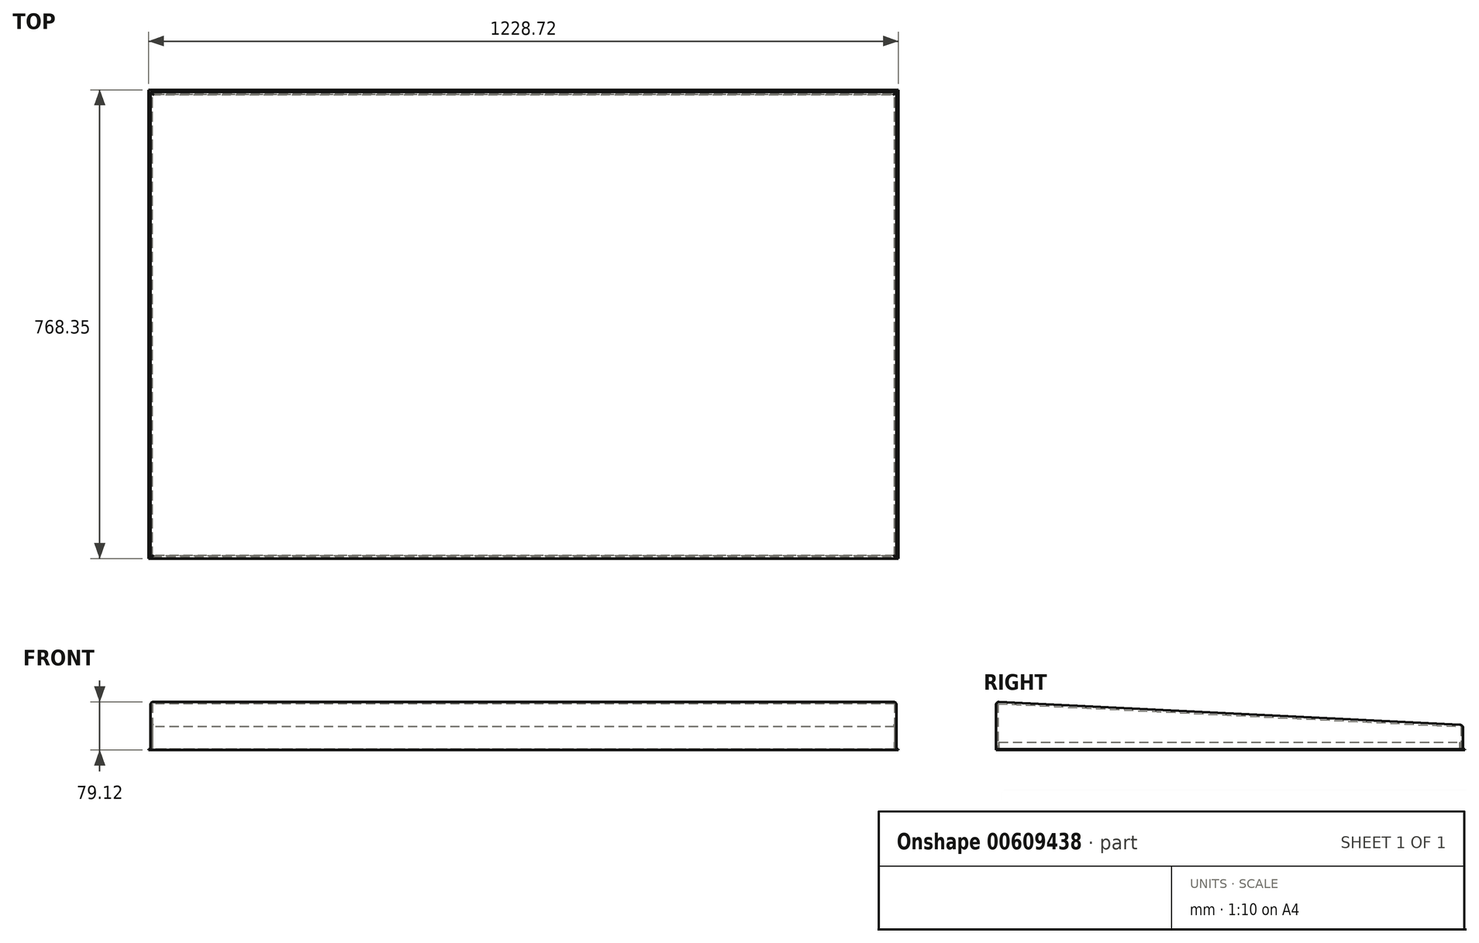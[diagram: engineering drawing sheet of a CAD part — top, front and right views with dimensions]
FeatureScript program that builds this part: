
annotation { "Feature Type Name" : "Feature", "Feature Type Description" : "" }
export const myFeature = defineFeature(function(context is Context, id is Id, definition is map)
    precondition{}
    {
        {
            var Q0;
            Q0=qCreatedBy(makeId("Top.planeOp"),FACE);
            var sketch = newSketch(context, id + "F0", { "sketchPlane" : qUnion([Q0])});
            skLineSegment(sketch, "E0.rect.bottom", {"start": v(611.19, 382.59) * mm, "end": v(-611.19, 382.59) * mm});
            skLineSegment(sketch, "E0.rect.top", {"start": v(611.19, -382.59) * mm, "end": v(-611.19, -382.59) * mm});
            skLineSegment(sketch, "E0.rect.left", {"start": v(611.19, 382.59) * mm, "end": v(611.19, -382.59) * mm});
            skLineSegment(sketch, "E0.rect.right", {"start": v(-611.19, 382.59) * mm, "end": v(-611.19, -382.59) * mm});
            skPoint(sketch, "E0.rect.middle", {"position": v(0, 0) * mm});
            skLineSegment(sketch, "E1.rect.bottom", {"start": v(-608.01, 379.41) * mm, "end": v(608.01, 379.41) * mm});
            skLineSegment(sketch, "E1.rect.top", {"start": v(-608.01, -379.41) * mm, "end": v(608.01, -379.41) * mm});
            skLineSegment(sketch, "E1.rect.left", {"start": v(-608.01, 379.41) * mm, "end": v(-608.01, -379.41) * mm});
            skLineSegment(sketch, "E1.rect.right", {"start": v(608.01, 379.41) * mm, "end": v(608.01, -379.41) * mm});
            skSolve(sketch);
        }
        {
            var Q0;
            Q0=makeQuery(id+"F0.imprint","IMPRINT",FACE,{"disambiguationData":[TD([[makeQuery(id+"F0.imprint","IMPRINT",EDGE,{"derivedFrom":sQuery(id+"F0.wireOp",EDGE,"E0.rect.bottom")}),1.0]])]});
            extrude(context, id + "F1", {"entities" : qUnion([Q0]), "depth" : 76.2 * mm});
        }
        {
            var Q0;
            Q0=makeQuery(id+"F1.opExtrude","SWEPT_FACE",FACE,{"disambiguationData":[OSD([sQuery(id+"F0.wireOp",EDGE,"E0.rect.left")])]});
            var sketch = newSketch(context, id + "F2", { "sketchPlane" : qUnion([Q0])});
            skLineSegment(sketch, "E2", {"start": v(-382.59, 76.2) * mm, "end": v(382.59, 38.1) * mm});
            skLineSegment(sketch, "E3", {"start": v(382.59, 38.1) * mm, "end": v(382.59, 76.2) * mm});
            skLineSegment(sketch, "E4", {"start": v(382.59, 76.2) * mm, "end": v(-382.59, 76.2) * mm});
            skSolve(sketch);
        }
        {
            var Q0;
            Q0=qSketchRegion(id+"F2",true);
            extrude(context, id + "F3", {"entities" : qUnion([Q0]), "operationType" : NewBodyOperationType.REMOVE, "oppositeDirection" : true, "depth" : 1270 * mm});
        }
        {
            var Q0;
            Q0=makeQuery(id+"F3.boolean.opBoolean","COPY",FACE,{"derivedFrom":makeQuery(id+"F3.opExtrude","SWEPT_FACE",FACE,{"disambiguationData":[OSD([sQuery(id+"F2.wireOp",EDGE,"E2")])]})});
            var sketch = newSketch(context, id + "F4", { "sketchPlane" : qUnion([Q0])});
            skLineSegment(sketch, "E5", {"start": v(611.19, -385.9) * mm, "end": v(-611.19, -385.9) * mm});
            skLineSegment(sketch, "E6", {"start": v(-611.19, -385.9) * mm, "end": v(-611.19, 380.22) * mm});
            skLineSegment(sketch, "E7", {"start": v(-611.19, 380.22) * mm, "end": v(611.19, 380.22) * mm});
            skLineSegment(sketch, "E8", {"start": v(611.19, 380.22) * mm, "end": v(611.19, -385.9) * mm});
            skSolve(sketch);
        }
        {
            var Q0;
            Q0=qSketchRegion(id+"F4",true);
            extrude(context, id + "F5", {"entities" : qUnion([Q0]), "operationType" : NewBodyOperationType.ADD, "depth" : 3.17 * mm});
        }
        {
            var Q0;
            Q0=qCreatedBy(makeId("Top.planeOp"),FACE);
            var sketch = newSketch(context, id + "F6", { "sketchPlane" : qUnion([Q0])});
            skLineSegment(sketch, "E9.bottom", {"start": v(-614.36, -382.59) * mm, "end": v(614.36, -382.59) * mm});
            skLineSegment(sketch, "E9.top", {"start": v(-614.36, 385.76) * mm, "end": v(614.36, 385.76) * mm});
            skLineSegment(sketch, "E9.left", {"start": v(-614.36, -382.59) * mm, "end": v(-614.36, 385.76) * mm});
            skLineSegment(sketch, "E9.right", {"start": v(614.36, -382.59) * mm, "end": v(614.36, 385.76) * mm});
            skSolve(sketch);
        }
        {
            var Q0;
            Q0=qSketchRegion(id+"F6",true);
            extrude(context, id + "F7", {"entities" : qUnion([Q0]), "operationType" : NewBodyOperationType.ADD, "depth" : 1.59 * mm});
        }
        {
            var Q0;
            Q0=makeQuery(id+"F7.boolean.opBoolean","MERGE",FACE,{"derivedFrom":[makeQuery(id+"F1.opExtrude","CAP_FACE",FACE,{"disambiguationData":[OSD([sQuery(id+"F0.wireOp",EDGE,"E0.rect.bottom"),sQuery(id+"F0.wireOp",EDGE,"E0.rect.top"),sQuery(id+"F0.wireOp",EDGE,"E0.rect.left"),sQuery(id+"F0.wireOp",EDGE,"E0.rect.right"),sQuery(id+"F0.wireOp",EDGE,"E1.rect.bottom"),sQuery(id+"F0.wireOp",EDGE,"E1.rect.top"),sQuery(id+"F0.wireOp",EDGE,"E1.rect.left"),sQuery(id+"F0.wireOp",EDGE,"E1.rect.right")])],"isStart":true}),makeQuery(id+"F7.opExtrude","CAP_FACE",FACE,{"disambiguationData":[OSD([sQuery(id+"F6.wireOp",EDGE,"E9.bottom"),sQuery(id+"F6.wireOp",EDGE,"E9.top"),sQuery(id+"F6.wireOp",EDGE,"E9.left"),sQuery(id+"F6.wireOp",EDGE,"E9.right")])],"isStart":true})]});
            var sketch = newSketch(context, id + "F8", { "sketchPlane" : qUnion([Q0])});
            skLineSegment(sketch, "E10.rect.bottom", {"start": v(-609.6, 377.83) * mm, "end": v(609.6, 377.83) * mm});
            skLineSegment(sketch, "E10.rect.top", {"start": v(-609.6, -377.83) * mm, "end": v(609.6, -377.83) * mm});
            skLineSegment(sketch, "E10.rect.left", {"start": v(-609.6, 377.83) * mm, "end": v(-609.6, -377.83) * mm});
            skLineSegment(sketch, "E10.rect.right", {"start": v(609.6, 377.83) * mm, "end": v(609.6, -377.83) * mm});
            skPoint(sketch, "E10.rect.middle", {"position": v(0, 0) * mm});
            skSolve(sketch);
        }
        {
            var Q0;
            Q0=qSketchRegion(id+"F8",true);
            extrude(context, id + "F9", {"entities" : qUnion([Q0]), "operationType" : NewBodyOperationType.REMOVE, "oppositeDirection" : true, "depth" : 12.7 * mm});
        }
        {
            var Q0;
            Q0=makeQuery(id+"F5.opExtrude","CAP_FACE",FACE,{"disambiguationData":[OSD([sQuery(id+"F4.wireOp",EDGE,"E5"),sQuery(id+"F4.wireOp",EDGE,"E6"),sQuery(id+"F4.wireOp",EDGE,"E7"),sQuery(id+"F4.wireOp",EDGE,"E8")])],"isStart":false});
            fillet(context, id + "F10", {"entities" : qUnion([Q0]), "radius" : 5.08 * mm, "tangentPropagation" : true, "allowEdgeOverflow" : false});
        }
    });
